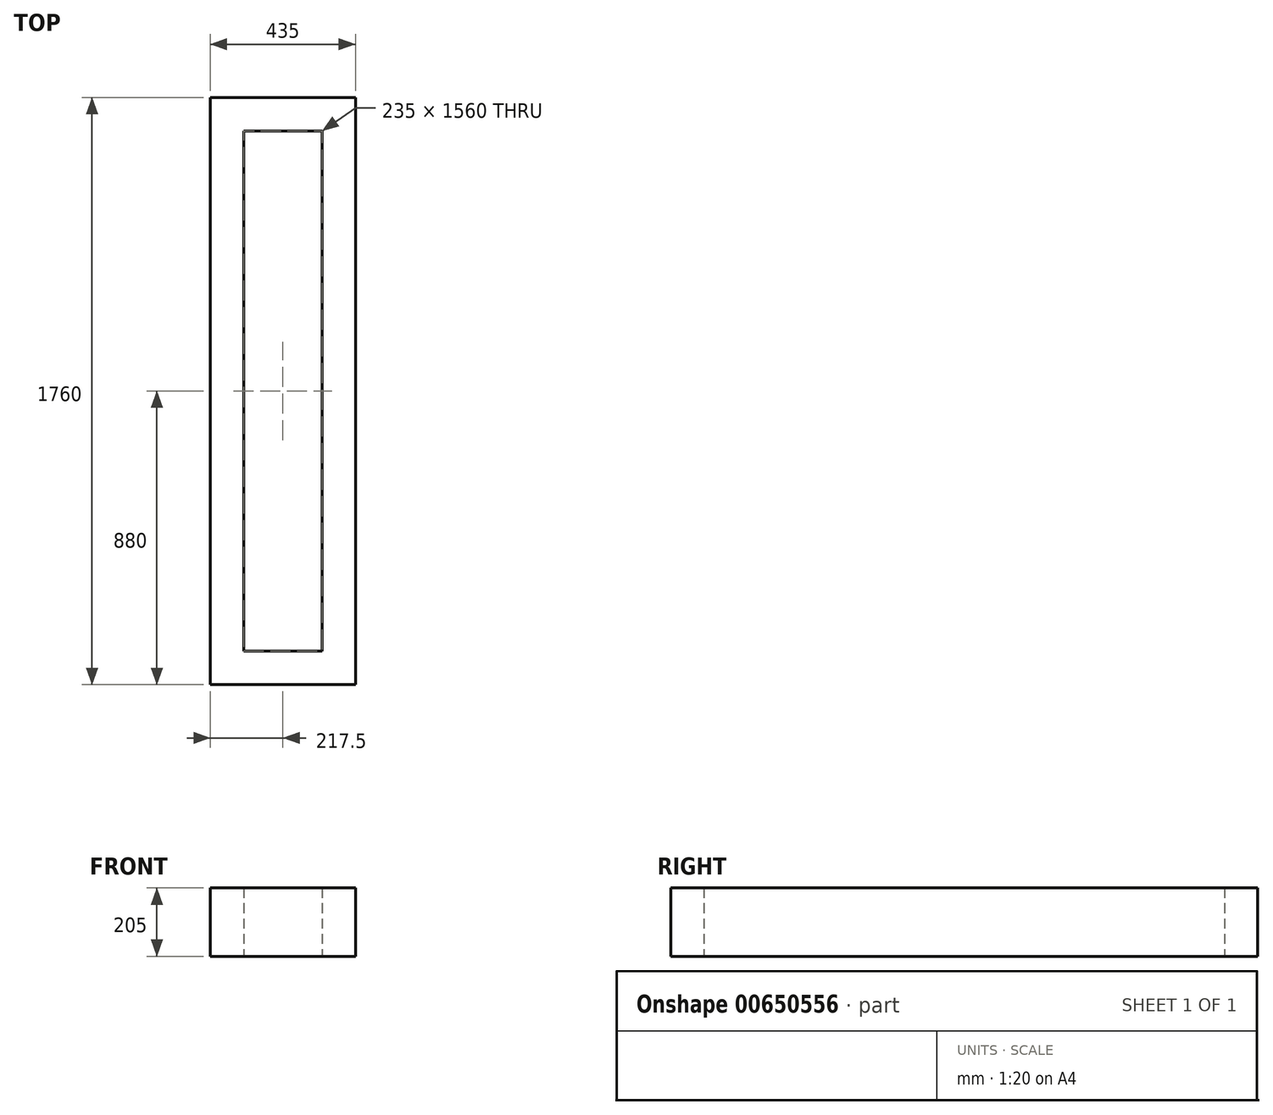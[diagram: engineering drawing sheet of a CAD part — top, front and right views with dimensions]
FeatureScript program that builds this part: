
annotation { "Feature Type Name" : "Feature", "Feature Type Description" : "" }
export const myFeature = defineFeature(function(context is Context, id is Id, definition is map)
    precondition{}
    {
        {
            var Q0;
            Q0=qCreatedBy(makeId("Top.planeOp"),FACE);
            var sketch = newSketch(context, id + "F0", { "sketchPlane" : qUnion([Q0]), "disableImprinting" : false});
            skLineSegment(sketch, "E0.bottom", {"start": v(0, 0) * mm, "end": v(-435, 0) * mm});
            skLineSegment(sketch, "E0.top", {"start": v(0, 1760) * mm, "end": v(-435, 1760) * mm});
            skLineSegment(sketch, "E0.left", {"start": v(0, 0) * mm, "end": v(0, 1760) * mm});
            skLineSegment(sketch, "E0.right", {"start": v(-435, 0) * mm, "end": v(-435, 1760) * mm});
            skLineSegment(sketch, "E1.bottom", {"start": v(-335, 1660) * mm, "end": v(-100, 1660) * mm});
            skLineSegment(sketch, "E1.top", {"start": v(-335, 100) * mm, "end": v(-100, 100) * mm});
            skLineSegment(sketch, "E1.left", {"start": v(-335, 1660) * mm, "end": v(-335, 100) * mm});
            skLineSegment(sketch, "E1.right", {"start": v(-100, 1660) * mm, "end": v(-100, 100) * mm});
            skSolve(sketch);
        }
        {
            var Q0;
            Q0=qSketchRegion(id+"F0",true);
            extrude(context, id + "F1", {"entities" : qUnion([Q0]), "depth" : 205 * mm, "offsetDistance" : 25 * mm});
        }
    });
